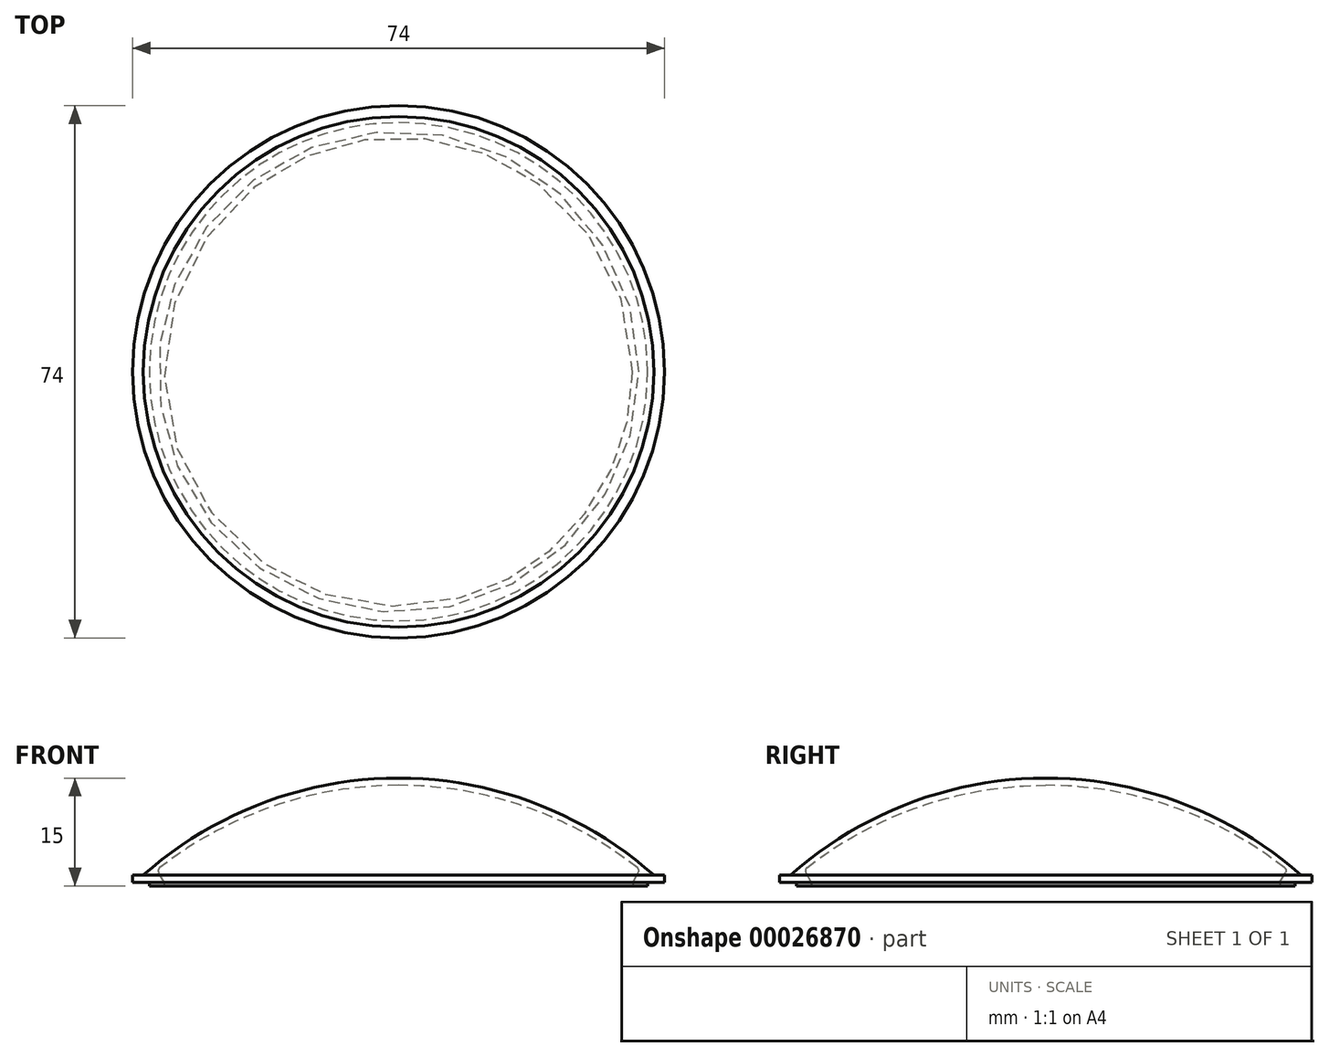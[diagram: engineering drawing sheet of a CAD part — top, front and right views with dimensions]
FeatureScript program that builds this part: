
annotation { "Feature Type Name" : "Feature", "Feature Type Description" : "" }
export const myFeature = defineFeature(function(context is Context, id is Id, definition is map)
    precondition{}
    {
        {
            var Q0;
            Q0=qCreatedBy(makeId("Front.planeOp"),FACE);
            var sketch = newSketch(context, id + "F0", { "sketchPlane" : qUnion([Q0])});
            skLineSegment(sketch, "E0", {"start": v(0, 22.2) * mm, "end": v(0, -9.6) * mm, "construction": true});
            skLineSegment(sketch, "E1", {"start": v(32.94, 0) * mm, "end": v(34.65, 0) * mm});
            skLineSegment(sketch, "E2", {"start": v(34.65, 0) * mm, "end": v(34.65, 0.5) * mm});
            skLineSegment(sketch, "E3", {"start": v(34.65, 0.5) * mm, "end": v(37, 0.5) * mm});
            skLineSegment(sketch, "E4", {"start": v(37, 0.5) * mm, "end": v(37, 1.5) * mm});
            skLineSegment(sketch, "E5", {"start": v(37, 1.5) * mm, "end": v(35.5, 1.5) * mm});
            skArc(sketch, "E6", {"start": v(35.5, 1.5) * mm, "mid": v(18.99, 11.5) * mm, "end": v(0, 15) * mm});
            skLineSegment(sketch, "E7", {"start": v(0, 15) * mm, "end": v(0, 14) * mm});
            skArc(sketch, "E8", {"start": v(33.23, 2.52) * mm, "mid": v(17.57, 11.03) * mm, "end": v(0, 14) * mm});
            skPoint(sketch, "E9.start.orphan", {"position": v(32, 1.5) * mm});
            skLineSegment(sketch, "E10", {"start": v(33.36, 1.89) * mm, "end": v(32.62, 0.54) * mm});
            skPoint(sketch, "E11.orphan", {"position": v(34.5, 1.5) * mm});
            skPoint(sketch, "E12.orphan", {"position": v(31.65, 0) * mm});
            skPoint(sketch, "E13.visualSharp", {"position": v(32.31, 0) * mm});
            skArc(sketch, "E13.filletArc", {"start": v(32.62, 0.54) * mm, "mid": v(32.62, 0.18) * mm, "end": v(32.94, 0) * mm});
            skPoint(sketch, "E14.visualSharp", {"position": v(33.57, 2.26) * mm});
            skArc(sketch, "E14.filletArc", {"start": v(33.36, 1.89) * mm, "mid": v(33.41, 2.23) * mm, "end": v(33.23, 2.52) * mm});
            skSolve(sketch);
        }
        {
            var Q0;
            Q0=makeQuery(id+"F0.imprint","IMPRINT",FACE,{"disambiguationData":[TD([[makeQuery(id+"F0.imprint","IMPRINT",EDGE,{"derivedFrom":sQuery(id+"F0.wireOp",EDGE,"E1")}),1.0]])]});
            var Q1;
            Q1=sQuery(id+"F0.wireOp",EDGE,"E0");
            revolve(context, id + "F1", {"entities" : qUnion([Q0]), "axis" : qUnion([Q1]), "revolveType" : RevolveType.FULL});
        }
    });
